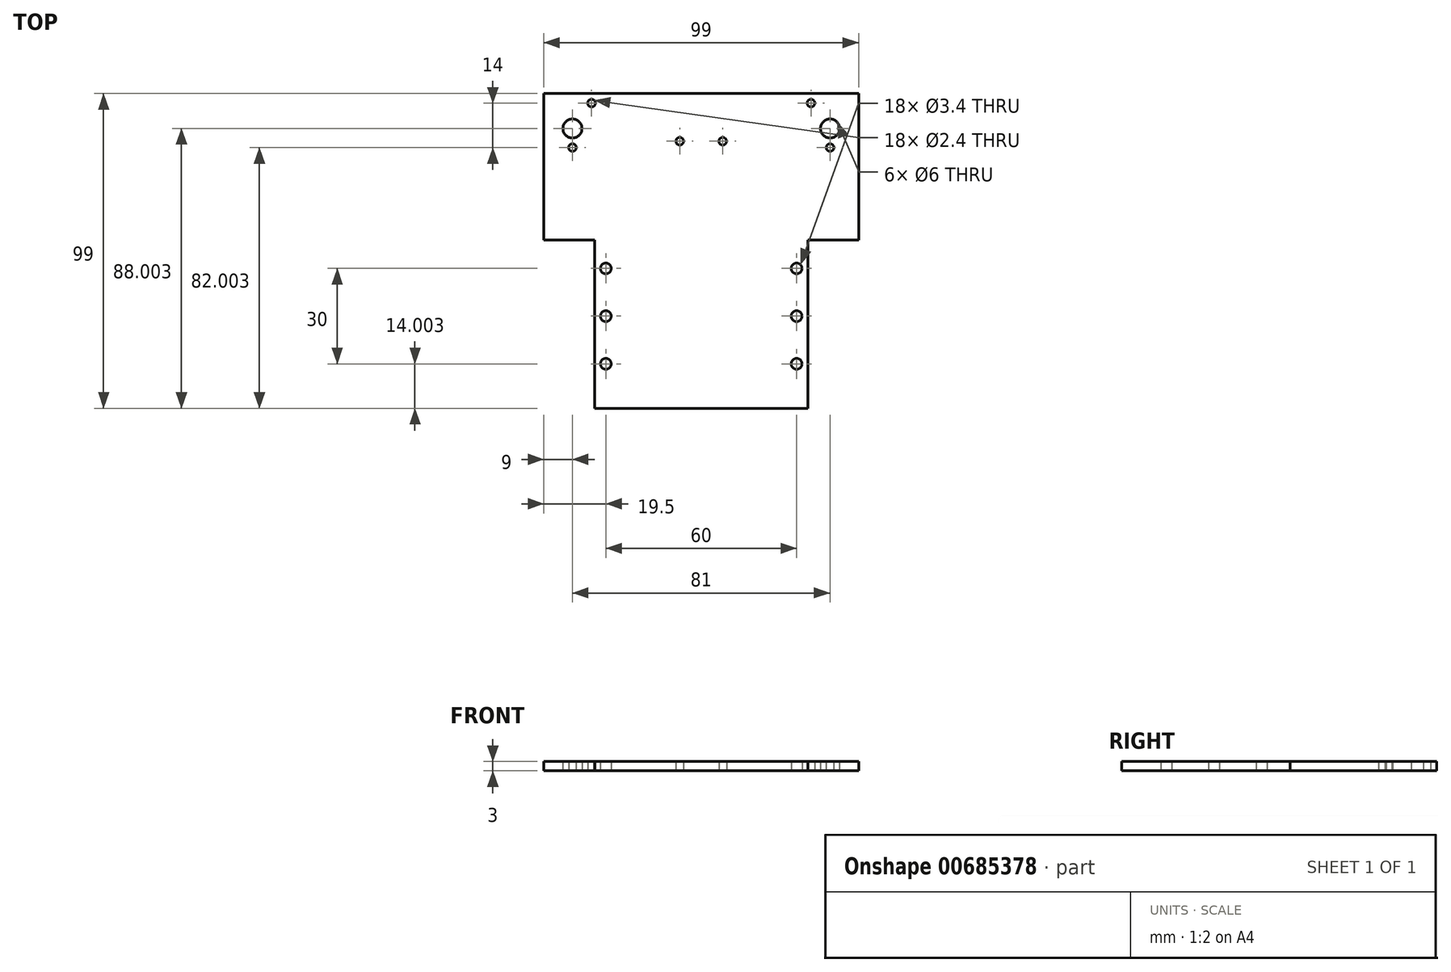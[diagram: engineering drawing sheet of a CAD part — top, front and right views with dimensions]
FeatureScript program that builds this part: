
annotation { "Feature Type Name" : "Feature", "Feature Type Description" : "" }
export const myFeature = defineFeature(function(context is Context, id is Id, definition is map)
    precondition{}
    {
        {
            var Q0;
            Q0=qCreatedBy(makeId("Top.planeOp"),FACE);
            var sketch = newSketch(context, id + "F0", { "sketchPlane" : qUnion([Q0])});
            skLineSegment(sketch, "E0", {"start": v(-49.5, 52.76) * mm, "end": v(-49.5, 6.76) * mm});
            skLineSegment(sketch, "E1", {"start": v(-49.5, 6.76) * mm, "end": v(-33.5, 6.76) * mm});
            skLineSegment(sketch, "E2", {"start": v(-33.5, 6.76) * mm, "end": v(-33.5, -46.24) * mm});
            skLineSegment(sketch, "E3", {"start": v(-33.5, -46.24) * mm, "end": v(0, -46.24) * mm});
            skLineSegment(sketch, "E4", {"start": v(-49.5, 52.76) * mm, "end": v(0, 52.76) * mm});
            skLineSegment(sketch, "E5.MirrorCS", {"start": v(49.5, 52.76) * mm, "end": v(0, 52.76) * mm});
            skLineSegment(sketch, "E6.MirrorCS", {"start": v(49.5, 52.76) * mm, "end": v(49.5, 6.76) * mm});
            skLineSegment(sketch, "E7.MirrorCS", {"start": v(49.5, 6.76) * mm, "end": v(33.5, 6.76) * mm});
            skLineSegment(sketch, "E8.MirrorCS", {"start": v(33.5, 6.76) * mm, "end": v(33.5, -46.24) * mm});
            skLineSegment(sketch, "E9.MirrorCS", {"start": v(33.5, -46.24) * mm, "end": v(0, -46.24) * mm});
            skCircle(sketch, "E10", {"center": v(-30, -32.24) * mm, "radius": 1.7 * mm});
            skCircle(sketch, "E11", {"center": v(-30, -17.24) * mm, "radius": 1.7 * mm});
            skCircle(sketch, "E12", {"center": v(-30, -2.24) * mm, "radius": 1.7 * mm});
            skCircle(sketch, "E13", {"center": v(-40.5, 41.76) * mm, "radius": 3 * mm});
            skCircle(sketch, "E14", {"center": v(-6.75, 37.76) * mm, "radius": 1.2 * mm});
            skCircle(sketch, "E15", {"center": v(-34.5, 49.76) * mm, "radius": 1.2 * mm});
            skCircle(sketch, "E16", {"center": v(-40.5, 35.76) * mm, "radius": 1.2 * mm});
            skCircle(sketch, "E17.MirrorC", {"center": v(6.75, 37.76) * mm, "radius": 1.2 * mm});
            skCircle(sketch, "E18.MirrorC", {"center": v(40.5, 41.76) * mm, "radius": 3 * mm});
            skCircle(sketch, "E19.MirrorC", {"center": v(34.5, 49.76) * mm, "radius": 1.2 * mm});
            skCircle(sketch, "E20.MirrorC", {"center": v(40.5, 35.76) * mm, "radius": 1.2 * mm});
            skCircle(sketch, "E21.MirrorC", {"center": v(30, -2.24) * mm, "radius": 1.7 * mm});
            skCircle(sketch, "E22.MirrorC", {"center": v(30, -17.24) * mm, "radius": 1.7 * mm});
            skCircle(sketch, "E23.MirrorC", {"center": v(30, -32.24) * mm, "radius": 1.7 * mm});
            skSolve(sketch);
        }
        {
            var Q0;
            Q0 = qSketchRegion(id + "F0", true);
            extrude(context, id + "F1", {"entities" : qUnion([Q0]), "depth" : 3 * mm, "offsetDistance" : 25 * mm});
        }
        {
            var Q0;
            Q0=makeQuery(id+"F1.opExtrude","CAP_FACE",FACE,{"disambiguationData":[OSD([sQuery(id+"F0.wireOp",EDGE,"E0"),sQuery(id+"F0.wireOp",EDGE,"E1"),sQuery(id+"F0.wireOp",EDGE,"E2"),sQuery(id+"F0.wireOp",EDGE,"E3"),sQuery(id+"F0.wireOp",EDGE,"E4"),sQuery(id+"F0.wireOp",EDGE,"E5.MirrorCS"),sQuery(id+"F0.wireOp",EDGE,"E6.MirrorCS"),sQuery(id+"F0.wireOp",EDGE,"E7.MirrorCS"),sQuery(id+"F0.wireOp",EDGE,"E8.MirrorCS"),sQuery(id+"F0.wireOp",EDGE,"E9.MirrorCS"),sQuery(id+"F0.wireOp",EDGE,"E10"),sQuery(id+"F0.wireOp",EDGE,"E11"),sQuery(id+"F0.wireOp",EDGE,"E12"),sQuery(id+"F0.wireOp",EDGE,"E13"),sQuery(id+"F0.wireOp",EDGE,"E14"),sQuery(id+"F0.wireOp",EDGE,"E15"),sQuery(id+"F0.wireOp",EDGE,"E16"),sQuery(id+"F0.wireOp",EDGE,"E17.MirrorC"),sQuery(id+"F0.wireOp",EDGE,"E18.MirrorC"),sQuery(id+"F0.wireOp",EDGE,"E19.MirrorC"),sQuery(id+"F0.wireOp",EDGE,"E20.MirrorC"),sQuery(id+"F0.wireOp",EDGE,"E21.MirrorC"),sQuery(id+"F0.wireOp",EDGE,"E22.MirrorC"),sQuery(id+"F0.wireOp",EDGE,"E23.MirrorC")])],"isStart":false});
            var sketch = newSketch(context, id + "F2", { "sketchPlane" : qUnion([Q0])});
            skSolve(sketch);
        }
        {
            var Q0;
            Q0=makeQuery(id+"F2.imprint","IMPRINT",FACE,{"disambiguationData":[TD([[makeQuery(id+"F2.imprint","IMPRINT",EDGE,{"derivedFrom":makeQuery(id+"F1.opExtrude","CAP_EDGE",EDGE,{"disambiguationData":[OSD([sQuery(id+"F0.wireOp",EDGE,"E0")])],"isStart":false})}),1.0]])]});
            var sketch = newSketch(context, id + "F3", { "sketchPlane" : qUnion([Q0])});
            skText(sketch, "E24", { "text": "GVB Fast!", "fontName": "OpenSans-Regular.ttf"});
            const initialGuessF3  = {"E24": [-0.0395, 0.0179, 1, 0, 0.01312]};
            skSetInitialGuess(sketch, initialGuessF3);
            skSolve(sketch);
        }
        {
            var Q0;
            Q0 = qSketchRegion(id + "F3", true);
            var Q1;
            Q1 = qSketchRegion(id + "F0", true);
            extrude(context, id + "F4", {"entities" : qUnion([Q0, Q1]), "operationType" : NewBodyOperationType.REMOVE, "oppositeDirection" : true, "depth" : 2 * mm, "offsetDistance" : 25 * mm});
        }
    });
